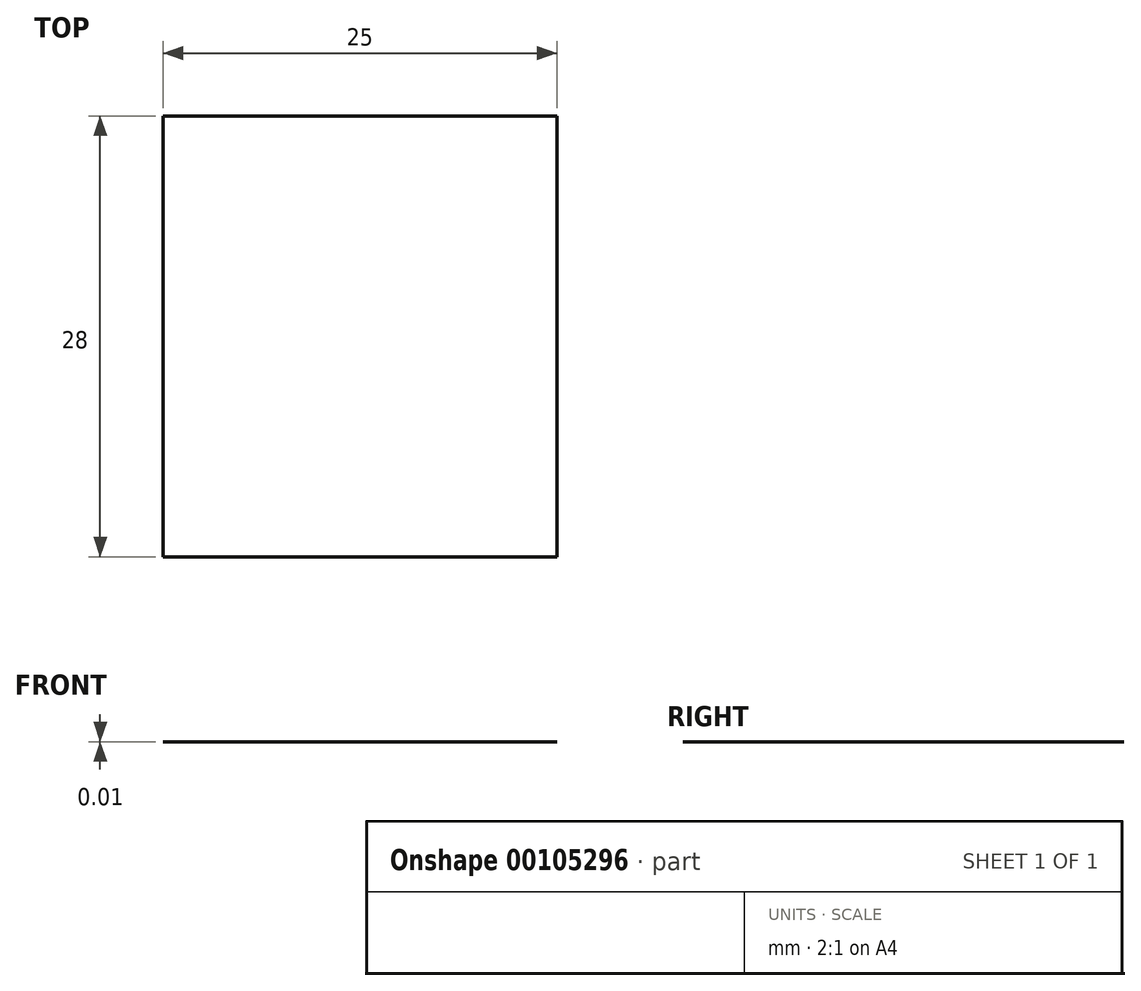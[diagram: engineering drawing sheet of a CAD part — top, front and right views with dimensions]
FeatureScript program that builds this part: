
annotation { "Feature Type Name" : "Feature", "Feature Type Description" : "" }
export const myFeature = defineFeature(function(context is Context, id is Id, definition is map)
    precondition{}
    {
        {
            var Q0;
            Q0=qCreatedBy(makeId("Top.planeOp"),FACE);
            var sketch = newSketch(context, id + "F0", { "sketchPlane" : qUnion([Q0])});
            skLineSegment(sketch, "E0.bottom", {"start": v(-12.9, 15.2) * mm, "end": v(12.1, 15.2) * mm});
            skLineSegment(sketch, "E0.top", {"start": v(-12.9, -12.8) * mm, "end": v(12.1, -12.8) * mm});
            skLineSegment(sketch, "E0.left", {"start": v(-12.9, 15.2) * mm, "end": v(-12.9, -12.8) * mm});
            skLineSegment(sketch, "E0.right", {"start": v(12.1, 15.2) * mm, "end": v(12.1, -12.8) * mm});
            skSolve(sketch);
        }
        {
            var Q0;
            Q0 = qSketchRegion(id + "F0", true);
            extrude(context, id + "F1", {"entities" : qUnion([Q0]), "depth" : 1 / 101.6 * mm});
        }
    });
